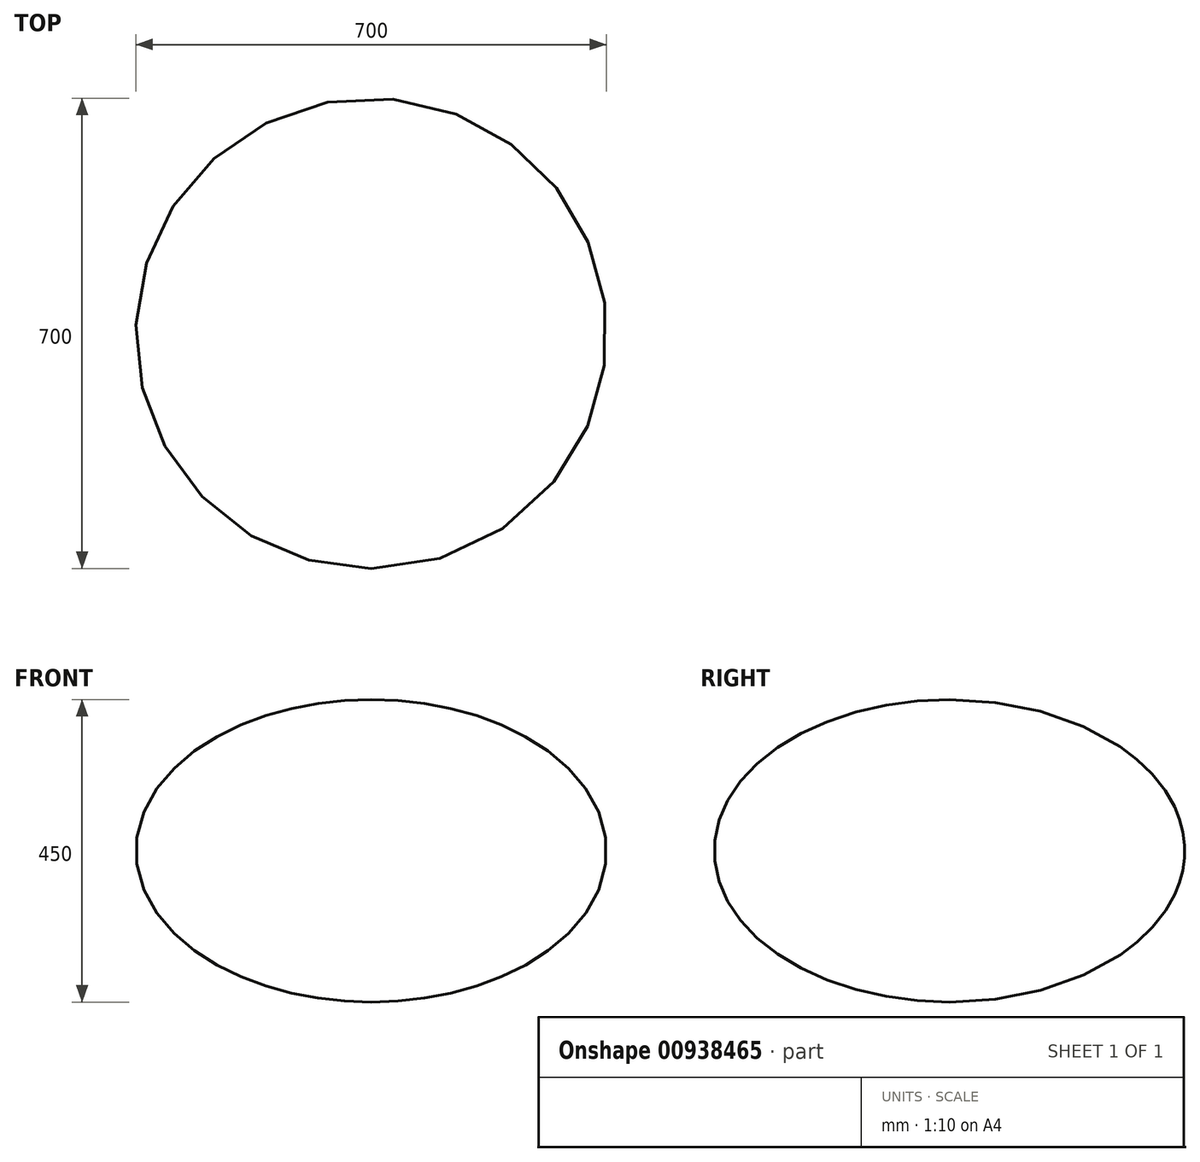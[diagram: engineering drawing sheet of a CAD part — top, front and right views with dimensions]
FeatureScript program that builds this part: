
annotation { "Feature Type Name" : "Feature", "Feature Type Description" : "" }
export const myFeature = defineFeature(function(context is Context, id is Id, definition is map)
    precondition{}
    {
        {
            var Q0;
            Q0=qCreatedBy(makeId("Right.planeOp"),FACE);
            var sketch = newSketch(context, id + "F0", { "sketchPlane" : qUnion([Q0])});
            skEllipticalArc(sketch, "E0", {});
            skPoint(sketch, "E1.startSnap0", {"position": v(0, 225) * mm});
            skLineSegment(sketch, "E2", {"start": v(0, 225) * mm, "end": v(0, -225) * mm});
            const initialGuessF0  = {"E0": [0, 0, -1, 0, 0.35, 0.225, 4.71238898038469, 1.5707963267948966]};
            skSetInitialGuess(sketch, initialGuessF0);
            skSolve(sketch);
        }
        {
            var Q0;
            Q0=makeQuery(id+"F0.imprint","IMPRINT",FACE,{"disambiguationData":[TD([[makeQuery(id+"F0.imprint","IMPRINT",EDGE,{"derivedFrom":sQuery(id+"F0.wireOp",EDGE,"E0")}),1.0]])]});
            var Q1;
            Q1=sQuery(id+"F0.wireOp",EDGE,"E2");
            revolve(context, id + "F1", {"surfaceOperationType" : NewSurfaceOperationType.NEW, "entities" : qUnion([Q0]), "axis" : qUnion([Q1]), "revolveType" : RevolveType.FULL});
        }
    });
